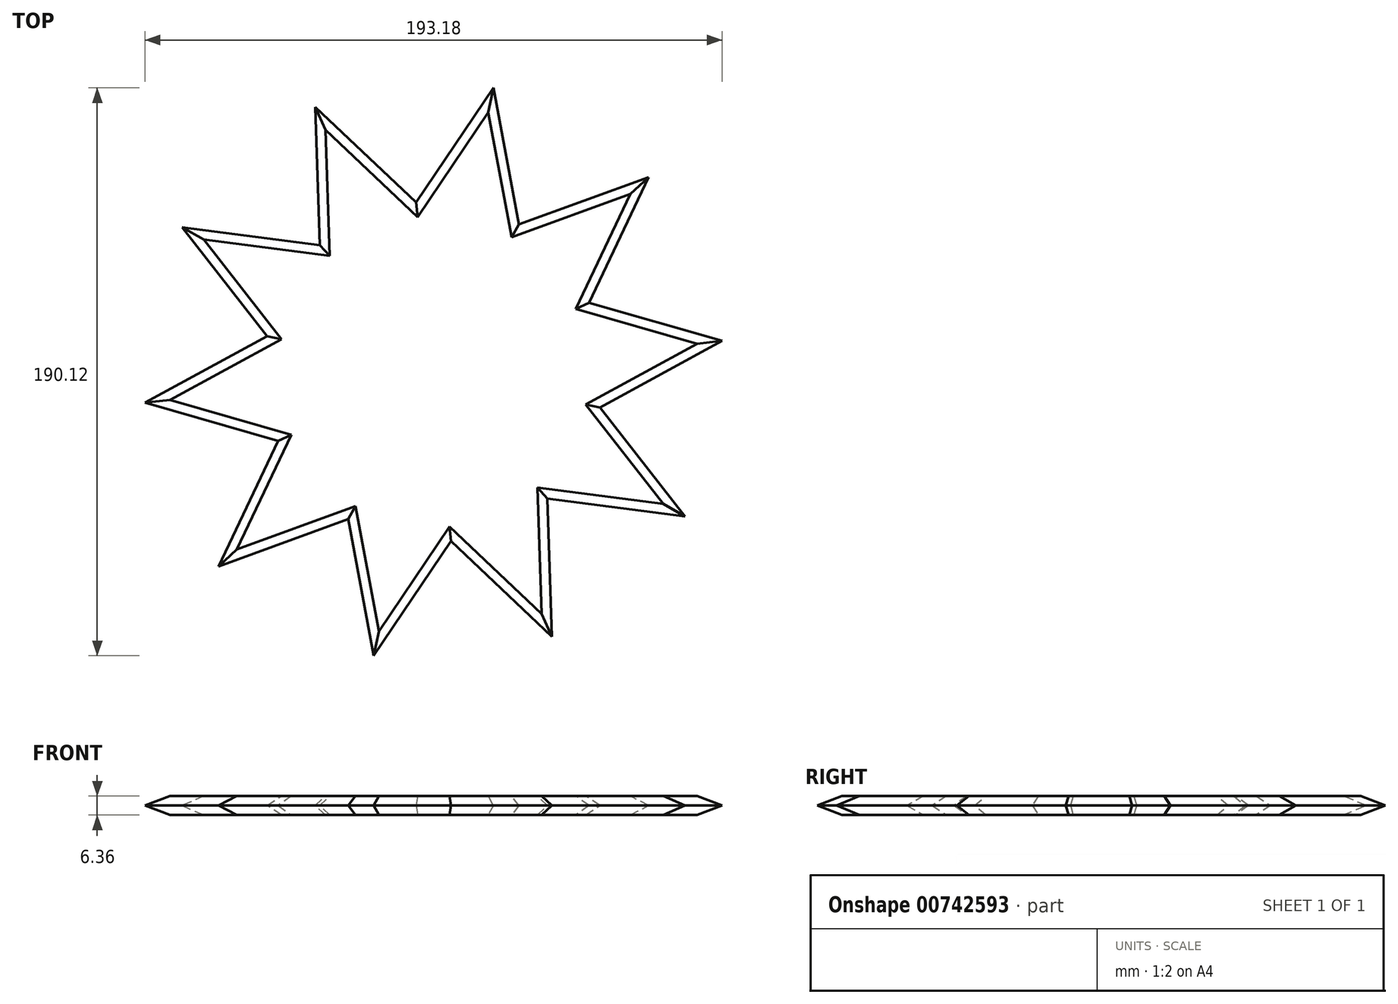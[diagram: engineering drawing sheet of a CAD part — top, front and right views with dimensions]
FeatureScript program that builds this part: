
annotation { "Feature Type Name" : "Feature", "Feature Type Description" : "" }
export const myFeature = defineFeature(function(context is Context, id is Id, definition is map)
    precondition{}
    {
        {
            var Q0;
            Q0=qCreatedBy(makeId("Top.planeOp"),FACE);
            var sketch = newSketch(context, id + "F0", { "sketchPlane" : qUnion([Q0])});
            skArc(sketch, "E0", {"start": v(-36.91, 9.43) * mm, "mid": v(24.74, -28.97) * mm, "end": v(-3.54, 37.94) * mm});
            skLineSegment(sketch, "E1", {"start": v(-39.69, 88.67) * mm, "end": v(-36.91, 9.43) * mm});
            skLineSegment(sketch, "E2", {"start": v(-39.69, 88.67) * mm, "end": v(19.44, 32.77) * mm});
            skLineSegment(sketch, "E3.1.0", {"start": v(-84.23, 48.4) * mm, "end": v(-35.4, -14.07) * mm});
            skLineSegment(sketch, "E3.1.1", {"start": v(-84.23, 48.4) * mm, "end": v(-3.54, 37.94) * mm});
            skLineSegment(sketch, "E3.2.0", {"start": v(-96.6, -10.34) * mm, "end": v(-20.37, -32.2) * mm});
            skLineSegment(sketch, "E3.2.1", {"start": v(-96.6, -10.34) * mm, "end": v(-25.16, 28.61) * mm});
            skLineSegment(sketch, "E3.3.0", {"start": v(-72.07, -65.14) * mm, "end": v(2.44, -38.02) * mm});
            skLineSegment(sketch, "E3.3.1", {"start": v(-72.07, -65.14) * mm, "end": v(-37.17, 8.36) * mm});
            skLineSegment(sketch, "E3.4.0", {"start": v(-20.01, -95.06) * mm, "end": v(24.32, -29.33) * mm});
            skLineSegment(sketch, "E3.4.1", {"start": v(-20.01, -95.06) * mm, "end": v(-34.99, -15.09) * mm});
            skLineSegment(sketch, "E3.5.0", {"start": v(39.69, -88.67) * mm, "end": v(36.91, -9.43) * mm});
            skLineSegment(sketch, "E3.5.1", {"start": v(39.69, -88.67) * mm, "end": v(-19.44, -32.77) * mm});
            skLineSegment(sketch, "E3.6.0", {"start": v(84.23, -48.4) * mm, "end": v(35.4, 14.07) * mm});
            skLineSegment(sketch, "E3.6.1", {"start": v(84.23, -48.4) * mm, "end": v(3.54, -37.94) * mm});
            skLineSegment(sketch, "E3.7.0", {"start": v(96.6, 10.34) * mm, "end": v(20.37, 32.2) * mm});
            skLineSegment(sketch, "E3.7.1", {"start": v(96.6, 10.34) * mm, "end": v(25.16, -28.61) * mm});
            skArc(sketch, "E4.trimOffspring", {"start": v(-24.32, 29.33) * mm, "mid": v(2.99, -37.98) * mm, "end": v(19.44, 32.77) * mm});
            skArc(sketch, "E5.trimOffspring", {"start": v(-35.4, -14.07) * mm, "mid": v(37.05, -8.9) * mm, "end": v(-25.16, 28.61) * mm});
            skArc(sketch, "E6.trimOffspring", {"start": v(-20.37, -32.2) * mm, "mid": v(35.2, 14.58) * mm, "end": v(-37.17, 8.36) * mm});
            skArc(sketch, "E7.trimOffspring", {"start": v(2.44, -38.02) * mm, "mid": v(19.9, 32.49) * mm, "end": v(-34.99, -15.09) * mm});
            skArc(sketch, "E8.trimOffspring", {"start": v(24.32, -29.33) * mm, "mid": v(-2.99, 37.98) * mm, "end": v(-19.44, -32.77) * mm});
            skArc(sketch, "E9.trimOffspring", {"start": v(36.91, -9.43) * mm, "mid": v(-24.74, 28.97) * mm, "end": v(3.54, -37.94) * mm});
            skArc(sketch, "E10.trimOffspring", {"start": v(35.4, 14.07) * mm, "mid": v(35.2, 14.58) * mm, "end": v(34.99, 15.09) * mm});
            skLineSegment(sketch, "E11.2.8.0", {"start": v(72.07, 65.14) * mm, "end": v(-2.44, 38.02) * mm});
            skLineSegment(sketch, "E11.3.8.0", {"start": v(72.07, 65.14) * mm, "end": v(37.17, -8.36) * mm});
            skLineSegment(sketch, "E11.2.9.0", {"start": v(20.01, 95.06) * mm, "end": v(-24.32, 29.33) * mm});
            skLineSegment(sketch, "E11.3.9.0", {"start": v(20.01, 95.06) * mm, "end": v(34.99, 15.09) * mm});
            skSolve(sketch);
        }
        {
            var Q0;
            {var subQ1=sQuery(id+"F0.wireOp",EDGE,"E0");var subQ3=sQuery(id+"F0.wireOp",EDGE,"E2");var subQ6=sQuery(id+"F0.wireOp",EDGE,"E3.1.1");var subQ8=sQuery(id+"F0.wireOp",EDGE,"E11.2.9.0");var subQ10=makeQuery(id+"F0.imprint","INTERSECT",VERTEX,{"derivedFrom":[subQ3,subQ8]});var subQ11=makeQuery(id+"F0.imprint","IMPRINT",EDGE,{"disambiguationData":[TD([[subQ10,-1.0]])],"derivedFrom":subQ3});var subQ13=sQuery(id+"F0.wireOp",EDGE,"E3.4.1");var subQ14=sQuery(id+"F0.wireOp",EDGE,"E3.3.0");var subQ15=makeQuery(id+"F0.imprint","INTERSECT",VERTEX,{"derivedFrom":[subQ14,subQ13]});var subQ16=sQuery(id+"F0.wireOp",EDGE,"E3.5.1");var subQ18=makeQuery(id+"F0.imprint","IMPRINT",EDGE,{"disambiguationData":[TD([[subQ15,-1.0]])],"derivedFrom":subQ14});var subQ19=sQuery(id+"F0.wireOp",EDGE,"E3.4.0");var subQ21=makeQuery(id+"F0.imprint","INTERSECT",VERTEX,{"derivedFrom":[subQ19,subQ16]});var subQ23=sQuery(id+"F0.wireOp",EDGE,"E3.2.1");var subQ24=sQuery(id+"F0.wireOp",EDGE,"E3.1.0");var subQ25=makeQuery(id+"F0.imprint","INTERSECT",VERTEX,{"derivedFrom":[subQ24,subQ23]});var subQ26=sQuery(id+"F0.wireOp",EDGE,"E1");var subQ29=sQuery(id+"F0.wireOp",EDGE,"E3.3.1");var subQ31=makeQuery(id+"F0.imprint","IMPRINT",EDGE,{"disambiguationData":[TD([[subQ25,-1.0]])],"derivedFrom":subQ24});var subQ35=sQuery(id+"F0.wireOp",EDGE,"E3.2.0");var subQ36=makeQuery(id+"F0.imprint","INTERSECT",VERTEX,{"derivedFrom":[subQ35,subQ29]});var subQ38=makeQuery(id+"F0.imprint","IMPRINT",EDGE,{"disambiguationData":[TD([[subQ36,-1.0]])],"derivedFrom":subQ35});var subQ42=makeQuery(id+"F0.imprint","INTERSECT",VERTEX,{"derivedFrom":[subQ1,subQ24]});var subQ45=makeQuery(id+"F0.imprint","INTERSECT",VERTEX,{"derivedFrom":[subQ1,subQ35]});var subQ47=sQuery(id+"F0.wireOp",EDGE,"E11.3.8.0");var subQ48=sQuery(id+"F0.wireOp",EDGE,"E3.7.0");var subQ49=makeQuery(id+"F0.imprint","INTERSECT",VERTEX,{"derivedFrom":[subQ48,subQ47]});var subQ52=makeQuery(id+"F0.imprint","IMPRINT",EDGE,{"disambiguationData":[TD([[subQ49,-1.0]])],"derivedFrom":subQ48});var subQ58=makeQuery(id+"F0.imprint","INTERSECT",VERTEX,{"derivedFrom":[subQ26,subQ6]});var subQ60=makeQuery(id+"F0.imprint","IMPRINT",EDGE,{"disambiguationData":[TD([[subQ58,-1.0]])],"derivedFrom":subQ26});var subQ63=sQuery(id+"F0.wireOp",EDGE,"E3.6.1");var subQ65=makeQuery(id+"F0.imprint","IMPRINT",EDGE,{"disambiguationData":[TD([[subQ21,-1.0]])],"derivedFrom":subQ19});var subQ66=makeQuery(id+"F0.imprint","INTERSECT",VERTEX,{"derivedFrom":[subQ1,subQ14]});var subQ68=sQuery(id+"F0.wireOp",EDGE,"E3.7.1");var subQ69=sQuery(id+"F0.wireOp",EDGE,"E3.6.0");var subQ70=makeQuery(id+"F0.imprint","INTERSECT",VERTEX,{"derivedFrom":[subQ69,subQ68]});var subQ72=makeQuery(id+"F0.imprint","IMPRINT",EDGE,{"disambiguationData":[TD([[subQ70,-1.0]])],"derivedFrom":subQ69});var subQ76=sQuery(id+"F0.wireOp",EDGE,"E3.5.0");var subQ77=makeQuery(id+"F0.imprint","INTERSECT",VERTEX,{"derivedFrom":[subQ76,subQ63]});var subQ79=makeQuery(id+"F0.imprint","INTERSECT",VERTEX,{"derivedFrom":[subQ1,subQ19]});var subQ82=makeQuery(id+"F0.imprint","IMPRINT",EDGE,{"disambiguationData":[TD([[subQ77,-1.0]])],"derivedFrom":subQ76});var subQ85=makeQuery(id+"F0.imprint","INTERSECT",VERTEX,{"derivedFrom":[subQ1,subQ69]});var subQ87=makeQuery(id+"F0.imprint","INTERSECT",VERTEX,{"derivedFrom":[subQ26,subQ3]});var subQ88=makeQuery(id+"F0.imprint","INTERSECT",VERTEX,{"derivedFrom":[subQ1,subQ76]});var subQ92=makeQuery(id+"F0.imprint","INTERSECT",VERTEX,{"derivedFrom":[subQ1,subQ3]});Q0=qUnion([makeQuery(id+"F0.imprint","IMPRINT",FACE,{"disambiguationData":[TD([[makeQuery(id+"F0.imprint","IMPRINT",EDGE,{"disambiguationData":[TD([[subQ92,1.0]])],"derivedFrom":subQ1}),-1.0]])]}),makeQuery(id+"F0.imprint","IMPRINT",FACE,{"disambiguationData":[TD([[subQ65,-1.0]])]}),makeQuery(id+"F0.imprint","IMPRINT",FACE,{"disambiguationData":[TD([[makeQuery(id+"F0.imprint","IMPRINT",EDGE,{"disambiguationData":[TD([[subQ88,-1.0]])],"derivedFrom":subQ1}),-1.0]])]}),makeQuery(id+"F0.imprint","IMPRINT",FACE,{"disambiguationData":[TD([[makeQuery(id+"F0.imprint","IMPRINT",EDGE,{"disambiguationData":[TD([[subQ87,-1.0]])],"derivedFrom":subQ26}),1.0]])]}),makeQuery(id+"F0.imprint","IMPRINT",FACE,{"disambiguationData":[TD([[makeQuery(id+"F0.imprint","IMPRINT",EDGE,{"disambiguationData":[TD([[subQ85,-1.0]])],"derivedFrom":subQ1}),-1.0]])]}),makeQuery(id+"F0.imprint","IMPRINT",FACE,{"disambiguationData":[TD([[subQ82,-1.0]])]}),makeQuery(id+"F0.imprint","IMPRINT",FACE,{"disambiguationData":[TD([[makeQuery(id+"F0.imprint","IMPRINT",EDGE,{"disambiguationData":[TD([[subQ79,-1.0]])],"derivedFrom":subQ1}),-1.0]])]}),makeQuery(id+"F0.imprint","IMPRINT",FACE,{"disambiguationData":[TD([[subQ60,-1.0]])]}),makeQuery(id+"F0.imprint","IMPRINT",FACE,{"disambiguationData":[TD([[subQ72,-1.0]])]}),makeQuery(id+"F0.imprint","IMPRINT",FACE,{"disambiguationData":[TD([[makeQuery(id+"F0.imprint","IMPRINT",EDGE,{"disambiguationData":[TD([[subQ66,-1.0]])],"derivedFrom":subQ1}),-1.0]])]}),makeQuery(id+"F0.imprint","IMPRINT",FACE,{"disambiguationData":[TD([[subQ11,1.0]])]}),makeQuery(id+"F0.imprint","IMPRINT",FACE,{"disambiguationData":[TD([[subQ60,1.0]])]}),makeQuery(id+"F0.imprint","IMPRINT",FACE,{"disambiguationData":[TD([[subQ52,-1.0]])]}),makeQuery(id+"F0.imprint","IMPRINT",FACE,{"disambiguationData":[TD([[makeQuery(id+"F0.imprint","IMPRINT",EDGE,{"disambiguationData":[TD([[subQ45,-1.0]])],"derivedFrom":subQ1}),-1.0]])]}),makeQuery(id+"F0.imprint","IMPRINT",FACE,{"disambiguationData":[TD([[subQ31,-1.0]])]}),makeQuery(id+"F0.imprint","IMPRINT",FACE,{"disambiguationData":[TD([[makeQuery(id+"F0.imprint","IMPRINT",EDGE,{"disambiguationData":[TD([[subQ42,-1.0]])],"derivedFrom":subQ1}),-1.0]])]}),makeQuery(id+"F0.imprint","IMPRINT",FACE,{"disambiguationData":[TD([[subQ38,-1.0]])]}),makeQuery(id+"F0.imprint","IMPRINT",FACE,{"disambiguationData":[TD([[subQ31,1.0]])]}),makeQuery(id+"F0.imprint","IMPRINT",FACE,{"disambiguationData":[TD([[subQ18,-1.0]])]}),makeQuery(id+"F0.imprint","IMPRINT",FACE,{"disambiguationData":[TD([[subQ11,-1.0]])]})]);}
            var Q1;
            {var subQ8=sQuery(id+"F0.wireOp",EDGE,"E5.trimOffspring");Q1=makeQuery(id+"F0.imprint","IMPRINT",FACE,{"disambiguationData":[TD([[makeQuery(id+"F0.imprint","IMPRINT",EDGE,{"derivedFrom":subQ8}),1.0]])]});}
            var Q2;
            {var subQ0=sQuery(id+"F0.wireOp",EDGE,"E5.trimOffspring");Q2=makeQuery(id+"F0.imprint","IMPRINT",FACE,{"disambiguationData":[TD([[makeQuery(id+"F0.imprint","IMPRINT",EDGE,{"derivedFrom":subQ0}),-1.0]])]});}
            var Q3;
            {var subQ0=sQuery(id+"F0.wireOp",EDGE,"E2");var subQ1=sQuery(id+"F0.wireOp",EDGE,"E0");var subQ2=makeQuery(id+"F0.imprint","INTERSECT",VERTEX,{"derivedFrom":[subQ1,subQ0]});Q3=makeQuery(id+"F0.imprint","IMPRINT",FACE,{"disambiguationData":[TD([[makeQuery(id+"F0.imprint","IMPRINT",EDGE,{"disambiguationData":[TD([[subQ2,-1.0]])],"derivedFrom":subQ1}),-1.0]])]});}
            var Q4;
            {var subQ0=sQuery(id+"F0.wireOp",EDGE,"E3.7.0");var subQ1=sQuery(id+"F0.wireOp",EDGE,"E0");var subQ2=makeQuery(id+"F0.imprint","INTERSECT",VERTEX,{"derivedFrom":[subQ1,subQ0]});Q4=makeQuery(id+"F0.imprint","IMPRINT",FACE,{"disambiguationData":[TD([[makeQuery(id+"F0.imprint","IMPRINT",EDGE,{"disambiguationData":[TD([[subQ2,1.0]])],"derivedFrom":subQ1}),-1.0]])]});}
            var Q5;
            {var subQ0=sQuery(id+"F0.wireOp",EDGE,"E3.6.0");var subQ1=sQuery(id+"F0.wireOp",EDGE,"E0");var subQ2=makeQuery(id+"F0.imprint","INTERSECT",VERTEX,{"derivedFrom":[subQ1,subQ0]});Q5=makeQuery(id+"F0.imprint","IMPRINT",FACE,{"disambiguationData":[TD([[makeQuery(id+"F0.imprint","IMPRINT",EDGE,{"disambiguationData":[TD([[subQ2,1.0]])],"derivedFrom":subQ1}),-1.0]])]});}
            var Q6;
            {var subQ0=sQuery(id+"F0.wireOp",EDGE,"E3.5.0");var subQ1=sQuery(id+"F0.wireOp",EDGE,"E0");var subQ2=makeQuery(id+"F0.imprint","INTERSECT",VERTEX,{"derivedFrom":[subQ1,subQ0]});Q6=makeQuery(id+"F0.imprint","IMPRINT",FACE,{"disambiguationData":[TD([[makeQuery(id+"F0.imprint","IMPRINT",EDGE,{"disambiguationData":[TD([[subQ2,1.0]])],"derivedFrom":subQ1}),-1.0]])]});}
            var Q7;
            {var subQ0=sQuery(id+"F0.wireOp",EDGE,"E3.4.0");var subQ1=sQuery(id+"F0.wireOp",EDGE,"E0");var subQ2=makeQuery(id+"F0.imprint","INTERSECT",VERTEX,{"derivedFrom":[subQ1,subQ0]});Q7=makeQuery(id+"F0.imprint","IMPRINT",FACE,{"disambiguationData":[TD([[makeQuery(id+"F0.imprint","IMPRINT",EDGE,{"disambiguationData":[TD([[subQ2,1.0]])],"derivedFrom":subQ1}),-1.0]])]});}
            var Q8;
            {var subQ0=sQuery(id+"F0.wireOp",EDGE,"E3.3.0");var subQ1=sQuery(id+"F0.wireOp",EDGE,"E0");var subQ2=makeQuery(id+"F0.imprint","INTERSECT",VERTEX,{"derivedFrom":[subQ1,subQ0]});Q8=makeQuery(id+"F0.imprint","IMPRINT",FACE,{"disambiguationData":[TD([[makeQuery(id+"F0.imprint","IMPRINT",EDGE,{"disambiguationData":[TD([[subQ2,1.0]])],"derivedFrom":subQ1}),-1.0]])]});}
            var Q9;
            {var subQ0=sQuery(id+"F0.wireOp",EDGE,"E3.2.0");var subQ1=sQuery(id+"F0.wireOp",EDGE,"E0");var subQ2=makeQuery(id+"F0.imprint","INTERSECT",VERTEX,{"derivedFrom":[subQ1,subQ0]});Q9=makeQuery(id+"F0.imprint","IMPRINT",FACE,{"disambiguationData":[TD([[makeQuery(id+"F0.imprint","IMPRINT",EDGE,{"disambiguationData":[TD([[subQ2,1.0]])],"derivedFrom":subQ1}),-1.0]])]});}
            var Q10;
            {var subQ0=sQuery(id+"F0.wireOp",EDGE,"E3.1.0");var subQ1=sQuery(id+"F0.wireOp",EDGE,"E0");var subQ2=makeQuery(id+"F0.imprint","INTERSECT",VERTEX,{"derivedFrom":[subQ1,subQ0]});Q10=makeQuery(id+"F0.imprint","IMPRINT",FACE,{"disambiguationData":[TD([[makeQuery(id+"F0.imprint","IMPRINT",EDGE,{"disambiguationData":[TD([[subQ2,1.0]])],"derivedFrom":subQ1}),-1.0]])]});}
            var Q11;
            {var subQ0=sQuery(id+"F0.wireOp",EDGE,"E4.trimOffspring");var subQ3=sQuery(id+"F0.wireOp",EDGE,"E3.2.1");var subQ5=makeQuery(id+"F0.imprint","INTERSECT",VERTEX,{"derivedFrom":[subQ3,subQ0]});Q11=makeQuery(id+"F0.imprint","IMPRINT",FACE,{"disambiguationData":[TD([[makeQuery(id+"F0.imprint","IMPRINT",EDGE,{"disambiguationData":[TD([[subQ5,1.0]])],"derivedFrom":subQ3}),-1.0]])]});}
            extrude(context, id + "F1", {"entities" : qUnion([Q0, Q1, Q2, Q3, Q4, Q5, Q6, Q7, Q8, Q9, Q10, Q11]), "endBound" : BoundingType.SYMMETRIC, "depth" : 6.35 * mm, "offsetDistance" : 25.4 * mm});
        }
        {
            var Q0;
            Q0=makeQuery(id+"F1.opExtrude","CAP_FACE",FACE,{"disambiguationData":[OSD([sQuery(id+"F0.wireOp",EDGE,"E1"),sQuery(id+"F0.wireOp",EDGE,"E2"),sQuery(id+"F0.wireOp",EDGE,"E3.1.0"),sQuery(id+"F0.wireOp",EDGE,"E3.1.1"),sQuery(id+"F0.wireOp",EDGE,"E3.2.0"),sQuery(id+"F0.wireOp",EDGE,"E3.2.1"),sQuery(id+"F0.wireOp",EDGE,"E3.3.0"),sQuery(id+"F0.wireOp",EDGE,"E3.3.1"),sQuery(id+"F0.wireOp",EDGE,"E3.4.0"),sQuery(id+"F0.wireOp",EDGE,"E3.4.1"),sQuery(id+"F0.wireOp",EDGE,"E3.5.0"),sQuery(id+"F0.wireOp",EDGE,"E3.5.1"),sQuery(id+"F0.wireOp",EDGE,"E3.6.0"),sQuery(id+"F0.wireOp",EDGE,"E3.6.1"),sQuery(id+"F0.wireOp",EDGE,"E3.7.0"),sQuery(id+"F0.wireOp",EDGE,"E3.7.1"),sQuery(id+"F0.wireOp",EDGE,"E11.2.8.0"),sQuery(id+"F0.wireOp",EDGE,"E11.3.8.0"),sQuery(id+"F0.wireOp",EDGE,"E11.2.9.0"),sQuery(id+"F0.wireOp",EDGE,"E11.3.9.0")])],"isStart":false});
            var Q1;
            Q1=makeQuery(id+"F1.opExtrude","CAP_FACE",FACE,{"disambiguationData":[OSD([sQuery(id+"F0.wireOp",EDGE,"E1"),sQuery(id+"F0.wireOp",EDGE,"E2"),sQuery(id+"F0.wireOp",EDGE,"E3.1.0"),sQuery(id+"F0.wireOp",EDGE,"E3.1.1"),sQuery(id+"F0.wireOp",EDGE,"E3.2.0"),sQuery(id+"F0.wireOp",EDGE,"E3.2.1"),sQuery(id+"F0.wireOp",EDGE,"E3.3.0"),sQuery(id+"F0.wireOp",EDGE,"E3.3.1"),sQuery(id+"F0.wireOp",EDGE,"E3.4.0"),sQuery(id+"F0.wireOp",EDGE,"E3.4.1"),sQuery(id+"F0.wireOp",EDGE,"E3.5.0"),sQuery(id+"F0.wireOp",EDGE,"E3.5.1"),sQuery(id+"F0.wireOp",EDGE,"E3.6.0"),sQuery(id+"F0.wireOp",EDGE,"E3.6.1"),sQuery(id+"F0.wireOp",EDGE,"E3.7.0"),sQuery(id+"F0.wireOp",EDGE,"E3.7.1"),sQuery(id+"F0.wireOp",EDGE,"E11.2.8.0"),sQuery(id+"F0.wireOp",EDGE,"E11.3.8.0"),sQuery(id+"F0.wireOp",EDGE,"E11.2.9.0"),sQuery(id+"F0.wireOp",EDGE,"E11.3.9.0")])],"isStart":true});
            chamfer(context, id + "F2", {"entities" : qUnion([Q0, Q1]), "width" : 3.17 * mm, "tangentPropagation" : true});
        }
    });
